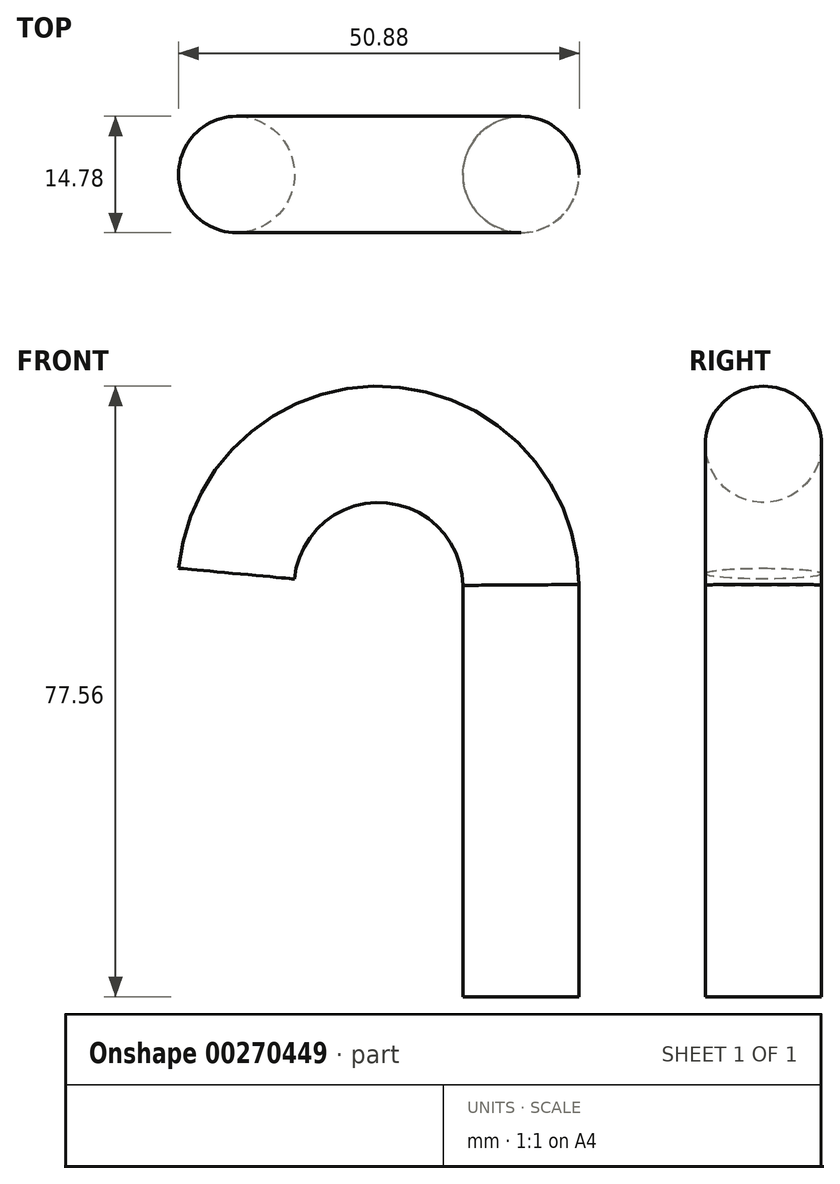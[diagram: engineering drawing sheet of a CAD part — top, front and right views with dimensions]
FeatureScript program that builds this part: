
annotation { "Feature Type Name" : "Feature", "Feature Type Description" : "" }
export const myFeature = defineFeature(function(context is Context, id is Id, definition is map)
    precondition{}
    {
        {
            var Q0;
            Q0=qCreatedBy(makeId("Front.planeOp"),FACE);
            var sketch = newSketch(context, id + "F0", { "sketchPlane" : qUnion([Q0])});
            skLineSegment(sketch, "E0", {"start": v(0, 0) * mm, "end": v(0, 52.3) * mm});
            skArc(sketch, "E1", {"start": v(0, 52.3) * mm, "mid": v(-17.39, 70.16) * mm, "end": v(-36.14, 53.74) * mm});
            skSolve(sketch);
        }
        {
            var Q0;
            Q0=qCreatedBy(makeId("Top.planeOp"),FACE);
            var sketch = newSketch(context, id + "F1", { "sketchPlane" : qUnion([Q0])});
            skCircle(sketch, "E2", {"center": v(0, 0) * mm, "radius": 7.39 * mm});
            skSolve(sketch);
        }
        {
            var Q0;
            Q0=makeQuery(id+"F1.imprint","IMPRINT",FACE,{"disambiguationData":[TD([[makeQuery(id+"F1.imprint","IMPRINT",EDGE,{"derivedFrom":sQuery(id+"F1.wireOp",EDGE,"E2")}),1.0]])]});
            var Q1;
            Q1=sQuery(id+"F0.wireOp",EDGE,"E0");
            var Q2;
            Q2=sQuery(id+"F0.wireOp",EDGE,"E1");
            sweep(context, id + "F2", {"profiles" : qUnion([Q0]), "path" : qUnion([Q1, Q2])});
        }
    });
